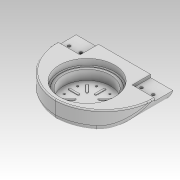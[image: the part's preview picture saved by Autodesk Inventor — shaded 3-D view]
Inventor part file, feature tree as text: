
AUTODESK INVENTOR PART (.ipt)
format: ipt  version: 2020 (Build 240168000, 168)  size: 694,784 bytes
history: native  units: mm
features: sketch x15, extrude x14, fillet x4, projected_geometry x4, revolve x1, mirror x1, plane x1, pattern_circular x1, chamfer x1
ambient origin geometry x8: Origin, YZ Plane, XZ Plane, XY Plane, X Axis, Y Axis, Z Axis, Center Point
bodies: Solid1 (feature_tree)
feature tree (42):
  extrude  "Extrusion1"  Depth=170.0mm
  extrude  "Extrusion2"  Depth=33.0mm
  extrude  "Extrusion3"  Depth=12.0mm
  sketch  "Sketch4"  dims[d8=20.0mm d9=0.0mm d10=0.0mm]
  revolve  "Revolution1"  [1 undecoded]
  extrude  "Extrusion4"  Depth=47.55mm
  extrude  "Extrusion5"  Depth=3.0mm
  fillet  "Fillet1"  Radius=1.0mm
  extrude  "Extrusion8"  Depth=17.5mm
  mirror  "Mirror1"
  extrude  "Extrusion6"  TaperAngle=90.0deg  [1 undecoded]
  extrude  "Extrusion7"  Depth=0.6mm
  extrude  "Extrusion9"  Depth=7.0mm
  fillet  "Fillet3"  Radius=1.5mm
  fillet  "Fillet4"  Radius=1.5mm
  extrude  "Extrusion10"  Depth=2.0mm
  plane  "Work Plane1"
  extrude  "Extrusion11"  Depth=60.0mm
  pattern_circular  "Circular Pattern1"  Count=2  [1 undecoded]
  extrude  "Extrusion12"  Depth=104.0mm
  extrude  "Extrusion13"  TaperAngle=45.0deg  [1 undecoded]
  fillet  "Fillet5"  Radius=6.4mm
  extrude  "Extrusion14"  Depth=10.0mm TaperAngle=0.0deg
  chamfer  "Chamfer2"  Distance=10.0mm
  sketch  "Sketch1"  dims[d0=170.0mm d1=170.0mm]
  sketch  "Sketch2"  dims[d2=40.0mm d3=33.0mm]
  projected_geometry  "Projected Loop1"
  projected_geometry  "Projected Loop2"
  sketch  "Sketch3"  dims[d4=120.0mm d5=0.0mm d7=12.0mm]
  projected_geometry  "Projected Loop3"
  sketch  "Sketch5"  dims[d11=0.0mm d12=0.0mm d13=47.55mm]
  sketch  "Sketch6"  dims[d14=10.1mm d15=3.0mm d16=1.0mm]
  projected_geometry  "Projected Loop4"
  sketch  "Sketch7"  dims[d17=40.2mm d18=17.5mm]
  sketch  "Sketch8"  dims[d19=65.0mm d20=90.0deg]
  sketch  "Sketch9"  dims[d21=11.05mm d22=0.6mm]
  sketch  "Sketch10"  dims[d23=1.5mm d25=7.0mm d26=1.5mm d27=1.5mm]
  sketch  "Sketch11"  dims[d29=35.0mm d30=2.0mm]
  sketch  "Sketch12"  dims[d31=14.9mm d32=60.0mm d33=20.0mm]
  sketch  "Sketch13"  dims[d34=5.0mm d35=0.0mm d36=104.0mm]
  sketch  "Sketch14"  dims[d37=8.0mm d38=45.0deg d39=6.4mm]
  sketch  "Sketch15"  dims[d40=40.0mm d42=360.0deg d44=12.5mm d45=0.0mm d46=10.0mm d47=5.0mm d48=0.0mm d49=137.0mm d50=0.0mm d51=5.0mm d52=12.0mm d53=7.0mm d54=5.0mm d55=17.0mm d56=0.0mm d57=0.0mm d58=15.0mm d59=2.0mm d60=22.5mm d65=0.8mm d66=0.0mm d68=10.0mm d70=30.0mm d71=3.5mm d72=0.0mm d73=0.0mm d74=0.5mm d75=22.5deg d76=-2.0mm d77=6.0mm d78=2.0mm d79=0.0mm d80=80.0mm d81=360.0deg d83=1.0mm d84=1.0mm d85=0.5mm d86=0.0mm d87=15.0mm d88=15.0mm d89=15.0mm d90=5.0mm d91=10.0mm d92=0.0mm d93=2.0mm d97=0.3mm d98=0.2mm d99=0.2mm d100=0.3mm d101=10.0mm d102=0.0mm d103=0.5mm d104=2.0mm d105=45.0deg d106=8.0mm]
note: 4 required parameter values undecoded (feature->parameter linkage not recoverable at this tier; creation-order binding heuristic only, values carry confidence <= 0.55)